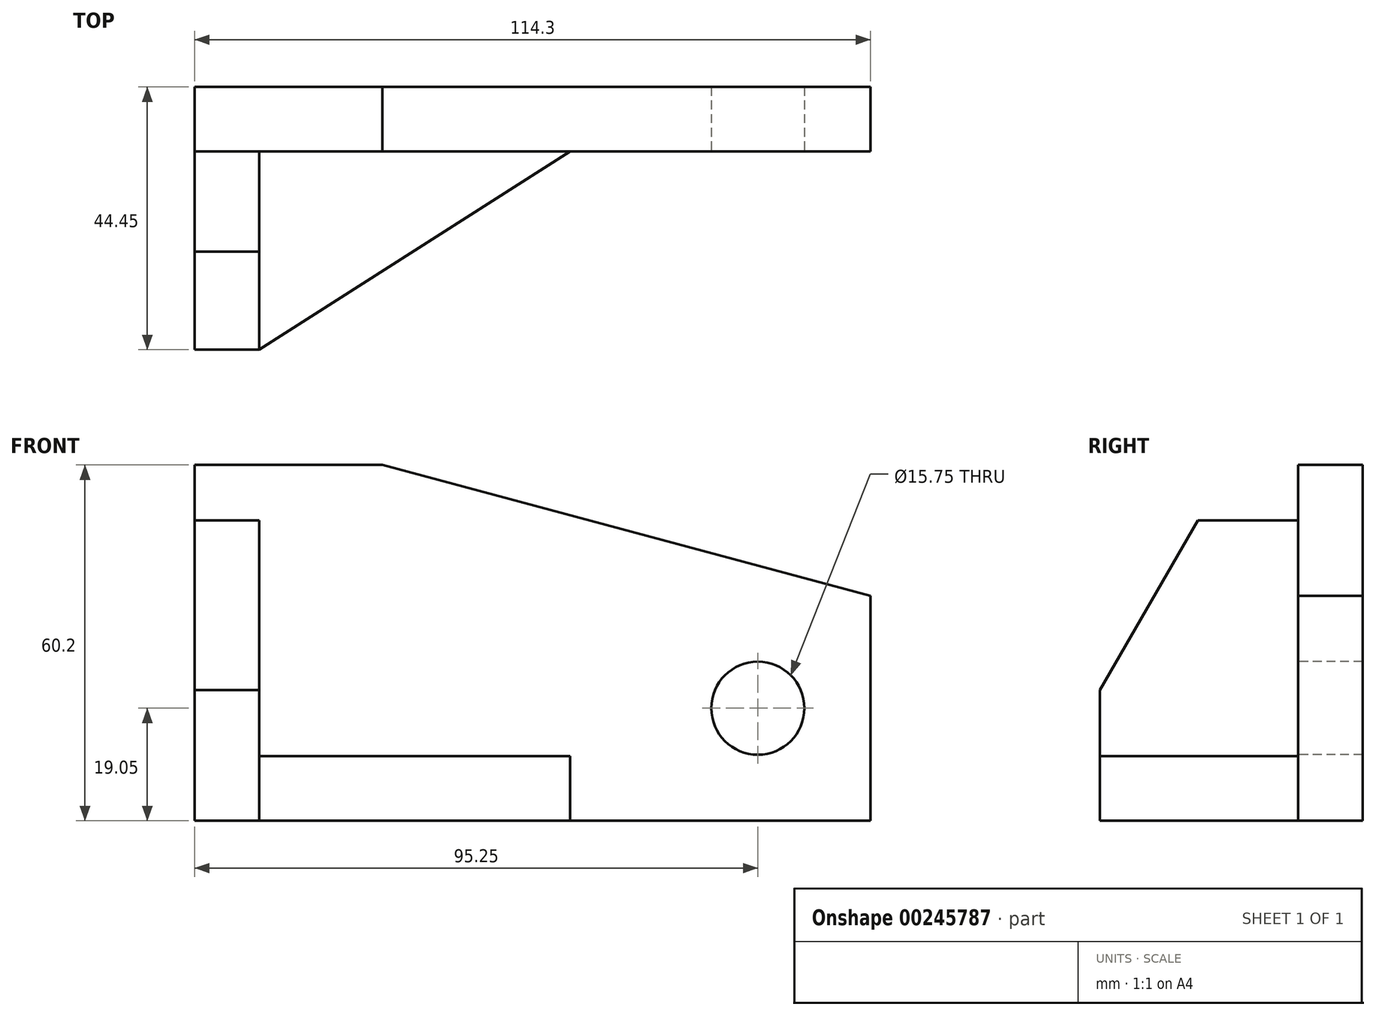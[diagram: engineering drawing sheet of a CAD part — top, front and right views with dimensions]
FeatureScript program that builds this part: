
annotation { "Feature Type Name" : "Feature", "Feature Type Description" : "" }
export const myFeature = defineFeature(function(context is Context, id is Id, definition is map)
    precondition{}
    {
        {
            var Q0;
            Q0=qCreatedBy(makeId("Top.planeOp"),FACE);
            var sketch = newSketch(context, id + "F0", { "sketchPlane" : qUnion([Q0])});
            skLineSegment(sketch, "E0", {"start": v(-55.2, -14.72) * mm, "end": v(-44.28, -14.72) * mm});
            skLineSegment(sketch, "E1", {"start": v(-55.2, -14.72) * mm, "end": v(-55.2, 29.73) * mm});
            skLineSegment(sketch, "E2", {"start": v(-55.2, 29.73) * mm, "end": v(59.1, 29.73) * mm});
            skLineSegment(sketch, "E3", {"start": v(59.1, 29.73) * mm, "end": v(59.1, 18.8) * mm});
            skLineSegment(sketch, "E4", {"start": v(59.1, 18.8) * mm, "end": v(8.3, 18.8) * mm});
            skLineSegment(sketch, "E5", {"start": v(8.3, 18.8) * mm, "end": v(-44.28, -14.72) * mm});
            skLineSegment(sketch, "E6", {"start": v(-44.28, -14.72) * mm, "end": v(-44.28, 18.8) * mm});
            skLineSegment(sketch, "E7", {"start": v(-44.28, 18.8) * mm, "end": v(8.3, 18.8) * mm});
            skLineSegment(sketch, "E8", {"start": v(-44.28, 18.8) * mm, "end": v(-55.2, 18.8) * mm});
            skSolve(sketch);
        }
        {
            var Q0;
            {var subQ0=sQuery(id+"F0.wireOp",EDGE,"E2");Q0=makeQuery(id+"F0.imprint","IMPRINT",FACE,{"disambiguationData":[TD([[makeQuery(id+"F0.imprint","IMPRINT",EDGE,{"derivedFrom":subQ0}),-1.0]])]});}
            extrude(context, id + "F1", {"entities" : qUnion([Q0]), "depth" : 60.2 * mm});
        }
        {
            var Q0;
            Q0=makeQuery(id+"F1.opExtrude","SWEPT_FACE",FACE,{"disambiguationData":[OSD([sQuery(id+"F0.wireOp",EDGE,"E4"),sQuery(id+"F0.wireOp",EDGE,"E7"),sQuery(id+"F0.wireOp",EDGE,"E8")])]});
            var sketch = newSketch(context, id + "F2", { "sketchPlane" : qUnion([Q0])});
            skLineSegment(sketch, "E9", {"start": v(-55.2, 60.2) * mm, "end": v(-23.45, 60.2) * mm});
            skLineSegment(sketch, "E10", {"start": v(-23.45, 60.2) * mm, "end": v(59.1, 38.08) * mm});
            skLineSegment(sketch, "E11", {"start": v(-23.45, 60.2) * mm, "end": v(59.1, 60.2) * mm});
            skLineSegment(sketch, "E12", {"start": v(59.1, 60.2) * mm, "end": v(59.1, 38.08) * mm});
            skLineSegment(sketch, "E13", {"start": v(59.1, 0) * mm, "end": v(40.05, 0) * mm});
            skLineSegment(sketch, "E14", {"start": v(40.05, 0) * mm, "end": v(40.05, 19.05) * mm});
            skCircle(sketch, "E15", {"center": v(40.05, 19.05) * mm, "radius": 7.87 * mm});
            skSolve(sketch);
        }
        {
            var Q0;
            Q0=makeQuery(id+"F2.imprint","IMPRINT",FACE,{"disambiguationData":[TD([[makeQuery(id+"F2.imprint","IMPRINT",EDGE,{"derivedFrom":sQuery(id+"F2.wireOp",EDGE,"E10")}),1.0]])]});
            var Q1;
            Q1=makeQuery(id+"F2.imprint","IMPRINT",FACE,{"disambiguationData":[TD([[makeQuery(id+"F2.imprint","IMPRINT",EDGE,{"derivedFrom":sQuery(id+"F2.wireOp",EDGE,"E15")}),1.0]])]});
            extrude(context, id + "F3", {"entities" : qUnion([Q0, Q1]), "operationType" : NewBodyOperationType.REMOVE, "endBound" : BoundingType.THROUGH_ALL, "oppositeDirection" : true, "depth" : 25.4 * mm});
        }
        {
            var Q0;
            Q0=makeQuery(id+"F1.opExtrude","SWEPT_FACE",FACE,{"disambiguationData":[OSD([sQuery(id+"F0.wireOp",EDGE,"E1")])]});
            var sketch = newSketch(context, id + "F4", { "sketchPlane" : qUnion([Q0])});
            skLineSegment(sketch, "E16", {"start": v(-18.8, 0) * mm, "end": v(14.72, 0) * mm});
            skLineSegment(sketch, "E17", {"start": v(14.72, 0) * mm, "end": v(14.72, 22.1) * mm});
            skLineSegment(sketch, "E18", {"start": v(-18.8, 0) * mm, "end": v(-18.8, 50.8) * mm});
            skLineSegment(sketch, "E19", {"start": v(-18.8, 50.8) * mm, "end": v(-1.85, 50.8) * mm});
            skLineSegment(sketch, "E20", {"start": v(14.72, 22.1) * mm, "end": v(-1.85, 50.8) * mm});
            skSolve(sketch);
        }
        {
            var Q0;
            Q0=makeQuery(id+"F4.imprint","IMPRINT",FACE,{"disambiguationData":[TD([[makeQuery(id+"F4.imprint","IMPRINT",EDGE,{"derivedFrom":sQuery(id+"F4.wireOp",EDGE,"E16")}),1.0]])]});
            extrude(context, id + "F5", {"entities" : qUnion([Q0]), "operationType" : NewBodyOperationType.ADD, "oppositeDirection" : true, "depth" : 10.92 * mm});
        }
        {
            var Q0;
            Q0=makeQuery(id+"F0.imprint","IMPRINT",FACE,{"disambiguationData":[TD([[makeQuery(id+"F0.imprint","IMPRINT",EDGE,{"derivedFrom":sQuery(id+"F0.wireOp",EDGE,"E5")}),-1.0]])]});
            extrude(context, id + "F6", {"entities" : qUnion([Q0]), "operationType" : NewBodyOperationType.ADD, "depth" : 10.92 * mm});
        }
    });
